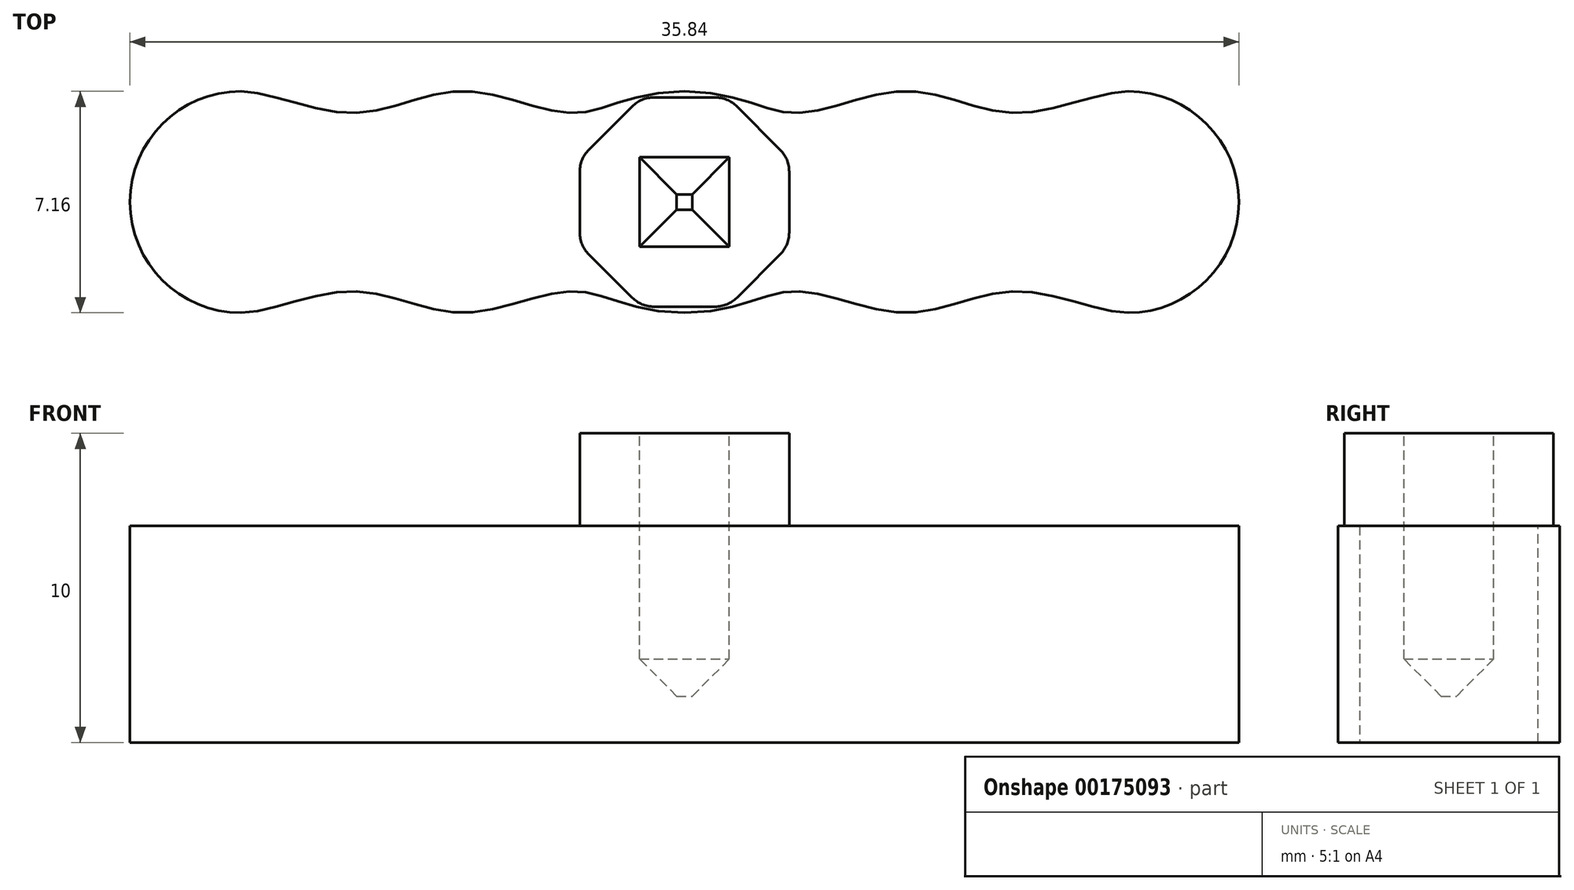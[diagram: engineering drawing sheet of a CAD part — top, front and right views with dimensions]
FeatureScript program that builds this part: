
annotation { "Feature Type Name" : "Feature", "Feature Type Description" : "" }
export const myFeature = defineFeature(function(context is Context, id is Id, definition is map)
    precondition{}
    {
        {
            assignVariable(context, id + "F0", {"name" : "r", "anyValue" : 2.6});
        }
        {
            assignVariable(context, id + "F1", {"name" : "d", "anyValue" : 8.5});
        }
        {
            var Q0;
            Q0=qCreatedBy(makeId("Top.planeOp"),FACE);
            var sketch = newSketch(context, id + "F2", { "sketchPlane" : qUnion([Q0])});
            skLineSegment(sketch, "E0", {"start": v(0, 0) * mm, "end": v(0, -3.58) * mm, "construction": true});
            skLineSegment(sketch, "E1", {"start": v(0, -2.88) * mm, "end": v(19.49, -2.88) * mm, "construction": true});
            skLineSegment(sketch, "E2", {"start": v(0, -3.58) * mm, "end": v(19.58, -3.58) * mm, "construction": true});
            skLineSegment(sketch, "E3.1.0.0", {"start": v(3.58, 0) * mm, "end": v(3.58, -3.58) * mm, "construction": true});
            skLineSegment(sketch, "E3.2.0.0", {"start": v(7.17, 0) * mm, "end": v(7.17, -3.58) * mm, "construction": true});
            skLineSegment(sketch, "E3.direction1", {"start": v(0, -3.58) * mm, "end": v(3.58, -3.58) * mm, "construction": true});
            skLineSegment(sketch, "E4.0.3.0", {"start": v(10.75, 0) * mm, "end": v(10.75, -3.58) * mm, "construction": true});
            skLineSegment(sketch, "E4.0.4.0", {"start": v(14.33, 0) * mm, "end": v(14.33, -3.58) * mm, "construction": true});
            skArc(sketch, "E5", {"start": v(14.33, -3.58) * mm, "mid": v(16.87, -2.53) * mm, "end": v(17.92, 0) * mm});
            skFitSpline(sketch, "E6", {"points": [v(0, -3.58) * mm, v(3.58, -2.88) * mm, v(7.17, -3.58) * mm, v(10.75, -2.88) * mm, v(14.33, -3.58) * mm], "startDerivative": vector(21.5, 0) * mm, "endDerivative": vector(11.48, 0) * mm});
            skLineSegment(sketch, "E7", {"start": v(-23.13, 0) * mm, "end": v(23.72, 0) * mm, "construction": true});
            skLineSegment(sketch, "E8", {"start": v(0, 13.7) * mm, "end": v(0, -14.93) * mm, "construction": true});
            skLineSegment(sketch, "E9.MirrorCS", {"start": v(10.75, 0) * mm, "end": v(10.75, 3.58) * mm, "construction": true});
            skLineSegment(sketch, "E10.MirrorCS", {"start": v(0, 3.58) * mm, "end": v(19.58, 3.58) * mm, "construction": true});
            skLineSegment(sketch, "E11.MirrorCS", {"start": v(0, 2.88) * mm, "end": v(19.49, 2.88) * mm, "construction": true});
            skLineSegment(sketch, "E12.MirrorCS", {"start": v(14.33, 0) * mm, "end": v(14.33, 3.58) * mm, "construction": true});
            skLineSegment(sketch, "E13.MirrorCS", {"start": v(0, 3.58) * mm, "end": v(3.58, 3.58) * mm, "construction": true});
            skArc(sketch, "E14.MirrorCS", {"start": v(14.33, 3.58) * mm, "mid": v(16.87, 2.53) * mm, "end": v(17.92, 0) * mm});
            skFitSpline(sketch, "E15.MirrorCS", {"points": [v(0, 3.58) * mm, v(3.58, 2.88) * mm, v(7.17, 3.58) * mm, v(10.75, 2.88) * mm, v(14.33, 3.58) * mm], "startDerivative": vector(21.5, 0) * mm, "endDerivative": vector(11.48, 0) * mm});
            skLineSegment(sketch, "E16.MirrorCS", {"start": v(3.58, 0) * mm, "end": v(3.58, 3.58) * mm, "construction": true});
            skLineSegment(sketch, "E17.MirrorCS", {"start": v(7.17, 0) * mm, "end": v(7.17, 3.58) * mm, "construction": true});
            skFitSpline(sketch, "E18.MirrorCS", {"points": [v(0, 3.58) * mm, v(-3.58, 2.88) * mm, v(-7.17, 3.58) * mm, v(-10.75, 2.88) * mm, v(-14.33, 3.58) * mm], "startDerivative": vector(-21.5, 0) * mm, "endDerivative": vector(-11.48, 0) * mm});
            skLineSegment(sketch, "E19.MirrorCS", {"start": v(0, 3.58) * mm, "end": v(-3.58, 3.58) * mm, "construction": true});
            skLineSegment(sketch, "E20.MirrorCS", {"start": v(-14.33, 0) * mm, "end": v(-14.33, 3.58) * mm, "construction": true});
            skLineSegment(sketch, "E21.MirrorCS", {"start": v(23.13, 0) * mm, "end": v(-23.72, 0) * mm, "construction": true});
            skLineSegment(sketch, "E22.MirrorCS", {"start": v(0, 3.58) * mm, "end": v(-19.58, 3.58) * mm, "construction": true});
            skLineSegment(sketch, "E23.MirrorCS", {"start": v(0, -3.58) * mm, "end": v(-3.58, -3.58) * mm, "construction": true});
            skLineSegment(sketch, "E24.MirrorCS", {"start": v(-14.33, 0) * mm, "end": v(-14.33, -3.58) * mm, "construction": true});
            skArc(sketch, "E25.MirrorCS", {"start": v(-14.33, 3.58) * mm, "mid": v(-16.87, 2.53) * mm, "end": v(-17.92, 0) * mm});
            skLineSegment(sketch, "E26.MirrorCS", {"start": v(0, -2.88) * mm, "end": v(-19.49, -2.88) * mm, "construction": true});
            skLineSegment(sketch, "E27.MirrorCS", {"start": v(0, -3.58) * mm, "end": v(-19.58, -3.58) * mm, "construction": true});
            skLineSegment(sketch, "E28.MirrorCS", {"start": v(-10.75, 0) * mm, "end": v(-10.75, -3.58) * mm, "construction": true});
            skArc(sketch, "E29.MirrorCS", {"start": v(-14.33, -3.58) * mm, "mid": v(-16.87, -2.53) * mm, "end": v(-17.92, 0) * mm});
            skLineSegment(sketch, "E30.MirrorCS", {"start": v(-3.58, 0) * mm, "end": v(-3.58, -3.58) * mm, "construction": true});
            skFitSpline(sketch, "E31.MirrorCS", {"points": [v(0, -3.58) * mm, v(-3.58, -2.88) * mm, v(-7.17, -3.58) * mm, v(-10.75, -2.88) * mm, v(-14.33, -3.58) * mm], "startDerivative": vector(-21.5, 0) * mm, "endDerivative": vector(-11.48, 0) * mm});
            skLineSegment(sketch, "E32.MirrorCS", {"start": v(-10.75, 0) * mm, "end": v(-10.75, 3.58) * mm, "construction": true});
            skLineSegment(sketch, "E33.MirrorCS", {"start": v(0, 2.88) * mm, "end": v(-19.49, 2.88) * mm, "construction": true});
            skLineSegment(sketch, "E34.MirrorCS", {"start": v(-3.58, 0) * mm, "end": v(-3.58, 3.58) * mm, "construction": true});
            skLineSegment(sketch, "E35.MirrorCS", {"start": v(-7.17, 0) * mm, "end": v(-7.17, 3.58) * mm, "construction": true});
            skLineSegment(sketch, "E36.MirrorCS", {"start": v(-7.17, 0) * mm, "end": v(-7.17, -3.58) * mm, "construction": true});
            skSolve(sketch);
        }
        {
            var Q0;
            Q0=qSketchRegion(id+"F2",true);
            extrude(context, id + "F3", {"entities" : qUnion([Q0]), "depth" : ((getVariable(context, 'd') + 1.5) * 0.7) * mm});
        }
        {
            var Q0;
            Q0=makeQuery(id+"F3.opExtrude","CAP_FACE",FACE,{"disambiguationData":[OSD([sQuery(id+"F2.wireOp",EDGE,"E5"),sQuery(id+"F2.wireOp",EDGE,"E6"),sQuery(id+"F2.wireOp",EDGE,"E14.MirrorCS"),sQuery(id+"F2.wireOp",EDGE,"E15.MirrorCS"),sQuery(id+"F2.wireOp",EDGE,"E18.MirrorCS"),sQuery(id+"F2.wireOp",EDGE,"E25.MirrorCS"),sQuery(id+"F2.wireOp",EDGE,"E29.MirrorCS"),sQuery(id+"F2.wireOp",EDGE,"E31.MirrorCS")])],"isStart":false});
            var sketch = newSketch(context, id + "F4", { "sketchPlane" : qUnion([Q0])});
            skCircle(sketch, "E37.cCircle", {"center": v(0, 0) * mm, "radius": 3.38 * mm, "construction": true});
            skLineSegment(sketch, "E37.0", {"start": v(0.99, -3.38) * mm, "end": v(-0.99, -3.38) * mm});
            skLineSegment(sketch, "E37.1", {"start": v(-1.7, -3.1) * mm, "end": v(-3.1, -1.7) * mm});
            skLineSegment(sketch, "E37.2", {"start": v(-3.38, -0.99) * mm, "end": v(-3.38, 0.99) * mm});
            skLineSegment(sketch, "E37.3", {"start": v(-3.1, 1.7) * mm, "end": v(-1.7, 3.1) * mm});
            skLineSegment(sketch, "E37.4", {"start": v(-0.99, 3.38) * mm, "end": v(0.99, 3.38) * mm});
            skLineSegment(sketch, "E37.5", {"start": v(1.7, 3.1) * mm, "end": v(3.1, 1.7) * mm});
            skLineSegment(sketch, "E37.6", {"start": v(3.38, 0.99) * mm, "end": v(3.38, -0.99) * mm});
            skLineSegment(sketch, "E37.7", {"start": v(3.1, -1.7) * mm, "end": v(1.7, -3.1) * mm});
            skPoint(sketch, "E37.0.midPoint", {"position": v(0, -3.38) * mm});
            skPoint(sketch, "E38.visualSharp", {"position": v(1.4, -3.38) * mm});
            skArc(sketch, "E38.filletArc", {"start": v(0.99, -3.38) * mm, "mid": v(1.37, -3.3) * mm, "end": v(1.7, -3.1) * mm});
            skPoint(sketch, "E39.visualSharp", {"position": v(-1.4, -3.38) * mm});
            skArc(sketch, "E39.filletArc", {"start": v(-1.7, -3.1) * mm, "mid": v(-1.37, -3.3) * mm, "end": v(-0.99, -3.38) * mm});
            skPoint(sketch, "E40.visualSharp", {"position": v(1.4, 3.38) * mm});
            skArc(sketch, "E40.filletArc", {"start": v(1.7, 3.1) * mm, "mid": v(1.37, 3.3) * mm, "end": v(0.99, 3.38) * mm});
            skPoint(sketch, "E41.visualSharp", {"position": v(-1.4, 3.38) * mm});
            skArc(sketch, "E41.filletArc", {"start": v(-0.99, 3.38) * mm, "mid": v(-1.37, 3.3) * mm, "end": v(-1.7, 3.1) * mm});
            skPoint(sketch, "E42.visualSharp", {"position": v(-3.38, 1.4) * mm});
            skArc(sketch, "E42.filletArc", {"start": v(-3.1, 1.7) * mm, "mid": v(-3.3, 1.37) * mm, "end": v(-3.38, 0.99) * mm});
            skPoint(sketch, "E43.visualSharp", {"position": v(-3.38, -1.4) * mm});
            skArc(sketch, "E43.filletArc", {"start": v(-3.38, -0.99) * mm, "mid": v(-3.3, -1.37) * mm, "end": v(-3.1, -1.7) * mm});
            skPoint(sketch, "E44.visualSharp", {"position": v(3.38, -1.4) * mm});
            skArc(sketch, "E44.filletArc", {"start": v(3.1, -1.7) * mm, "mid": v(3.3, -1.37) * mm, "end": v(3.38, -0.99) * mm});
            skPoint(sketch, "E45.visualSharp", {"position": v(3.38, 1.4) * mm});
            skArc(sketch, "E45.filletArc", {"start": v(3.38, 0.99) * mm, "mid": v(3.3, 1.37) * mm, "end": v(3.1, 1.7) * mm});
            skSolve(sketch);
        }
        {
            var Q0;
            Q0=qSketchRegion(id+"F4",true);
            extrude(context, id + "F5", {"entities" : qUnion([Q0]), "operationType" : NewBodyOperationType.ADD, "depth" : ((getVariable(context, 'd') + 1.5) * 0.3) * mm});
        }
        {
            var Q0;
            Q0=makeQuery(id+"F5.opExtrude","CAP_FACE",FACE,{"disambiguationData":[OSD([sQuery(id+"F4.wireOp",EDGE,"E37.0"),sQuery(id+"F4.wireOp",EDGE,"E37.1"),sQuery(id+"F4.wireOp",EDGE,"E37.2"),sQuery(id+"F4.wireOp",EDGE,"E37.3"),sQuery(id+"F4.wireOp",EDGE,"E37.4"),sQuery(id+"F4.wireOp",EDGE,"E37.5"),sQuery(id+"F4.wireOp",EDGE,"E37.6"),sQuery(id+"F4.wireOp",EDGE,"E37.7"),sQuery(id+"F4.wireOp",EDGE,"E38.filletArc"),sQuery(id+"F4.wireOp",EDGE,"E39.filletArc"),sQuery(id+"F4.wireOp",EDGE,"E40.filletArc"),sQuery(id+"F4.wireOp",EDGE,"E41.filletArc"),sQuery(id+"F4.wireOp",EDGE,"E42.filletArc"),sQuery(id+"F4.wireOp",EDGE,"E43.filletArc"),sQuery(id+"F4.wireOp",EDGE,"E44.filletArc"),sQuery(id+"F4.wireOp",EDGE,"E45.filletArc")])],"isStart":false});
            var sketch = newSketch(context, id + "F6", { "sketchPlane" : qUnion([Q0])});
            skLineSegment(sketch, "E46.bottom", {"start": v(-1.45, 1.45) * mm, "end": v(1.45, 1.45) * mm});
            skLineSegment(sketch, "E46.top", {"start": v(-1.45, -1.45) * mm, "end": v(1.45, -1.45) * mm});
            skLineSegment(sketch, "E46.left", {"start": v(-1.45, 1.45) * mm, "end": v(-1.45, -1.45) * mm});
            skLineSegment(sketch, "E46.right", {"start": v(1.45, 1.45) * mm, "end": v(1.45, -1.45) * mm});
            skLineSegment(sketch, "E47", {"start": v(1.45, 1.45) * mm, "end": v(-1.45, -1.45) * mm, "construction": true});
            skSolve(sketch);
        }
        {
            var Q0;
            Q0=qSketchRegion(id+"F6",true);
            extrude(context, id + "F7", {"entities" : qUnion([Q0]), "operationType" : NewBodyOperationType.REMOVE, "flatOperationType" : FlatOperationType.REMOVE, "oppositeDirection" : true, "offsetDistance" : 25 * mm, "depth" : (getVariable(context, 'd')) * mm, "domain" : OperationDomain.MODEL});
        }
        {
            var Q0;
            Q0=makeQuery(id+"F7.boolean.opBoolean","COPY",EDGE,{"derivedFrom":makeQuery(id+"F7.opExtrude","CAP_EDGE",EDGE,{"disambiguationData":[OSD([sQuery(id+"F6.wireOp",EDGE,"E46.top")])],"isStart":false})});
            var Q1;
            Q1=makeQuery(id+"F7.boolean.opBoolean","COPY",EDGE,{"derivedFrom":makeQuery(id+"F7.opExtrude","CAP_EDGE",EDGE,{"disambiguationData":[OSD([sQuery(id+"F6.wireOp",EDGE,"E46.right")])],"isStart":false})});
            var Q2;
            Q2=makeQuery(id+"F7.boolean.opBoolean","COPY",EDGE,{"derivedFrom":makeQuery(id+"F7.opExtrude","CAP_EDGE",EDGE,{"disambiguationData":[OSD([sQuery(id+"F6.wireOp",EDGE,"E46.bottom")])],"isStart":false})});
            var Q3;
            Q3=makeQuery(id+"F7.boolean.opBoolean","COPY",EDGE,{"derivedFrom":makeQuery(id+"F7.opExtrude","CAP_EDGE",EDGE,{"disambiguationData":[OSD([sQuery(id+"F6.wireOp",EDGE,"E46.left")])],"isStart":false})});
            chamfer(context, id + "F8", {"entities" : qUnion([Q0, Q1, Q2, Q3]), "width" : (getVariable(context, 'r') / 2 - 0.1) * mm, "tangentPropagation" : true});
        }
    });
